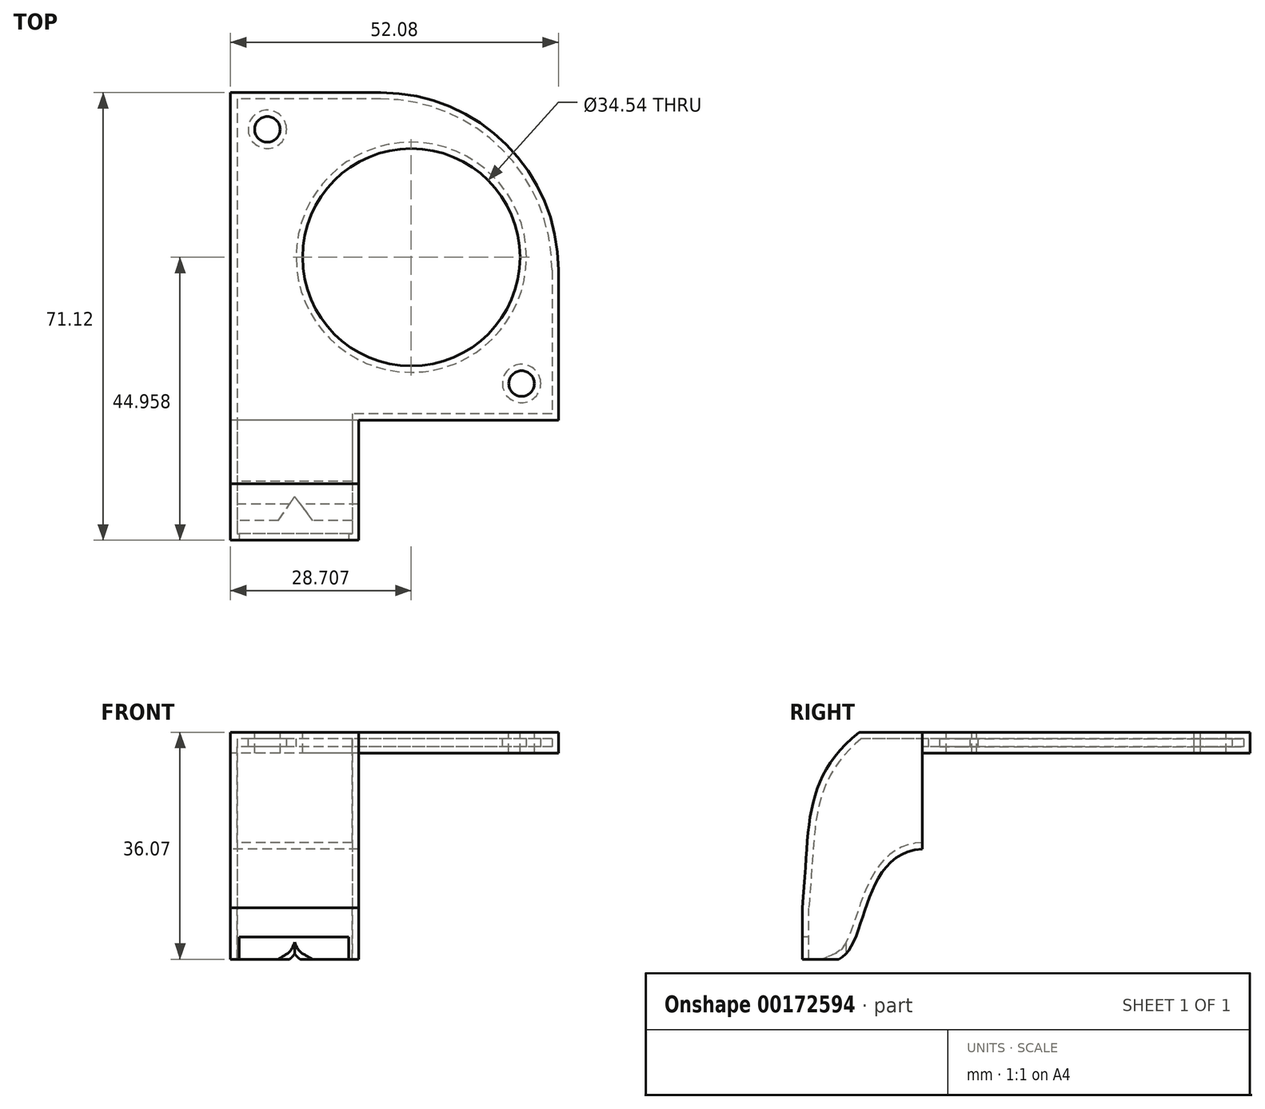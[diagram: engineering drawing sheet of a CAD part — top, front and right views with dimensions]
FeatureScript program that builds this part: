
annotation { "Feature Type Name" : "Feature", "Feature Type Description" : "" }
export const myFeature = defineFeature(function(context is Context, id is Id, definition is map)
    precondition{}
    {
        {
            var Q0;
            Q0=qCreatedBy(makeId("Front.planeOp"),FACE);
            var sketch = newSketch(context, id + "F0", { "sketchPlane" : qUnion([Q0])});
            skLineSegment(sketch, "E0.bottom", {"start": v(26.04, 1.65) * mm, "end": v(-26.04, 1.65) * mm});
            skLineSegment(sketch, "E0.top", {"start": v(26.04, -1.65) * mm, "end": v(-26.04, -1.65) * mm});
            skLineSegment(sketch, "E0.left", {"start": v(26.04, 1.65) * mm, "end": v(26.04, -1.65) * mm});
            skLineSegment(sketch, "E0.right", {"start": v(-26.04, 1.65) * mm, "end": v(-26.04, -1.65) * mm});
            skPoint(sketch, "E0.middle", {"position": v(0, 0) * mm});
            skLineSegment(sketch, "E1.bottom", {"start": v(-26.04, -1.65) * mm, "end": v(-5.71, -1.65) * mm});
            skLineSegment(sketch, "E1.top", {"start": v(-26.03, -34.67) * mm, "end": v(-5.71, -34.67) * mm});
            skLineSegment(sketch, "E1.left", {"start": v(-26.04, -1.65) * mm, "end": v(-26.04, -34.67) * mm});
            skLineSegment(sketch, "E1.right", {"start": v(-5.71, -1.65) * mm, "end": v(-5.71, -34.67) * mm});
            skPoint(sketch, "E2.middle", {"position": v(-15.87, -31.48) * mm});
            skPoint(sketch, "E2.middle.positionSnap0", {"position": v(-15.87, -34.67) * mm});
            skPoint(sketch, "E2.centerSnap0", {"position": v(-15.87, -34.67) * mm});
            skSolve(sketch);
        }
        {
            var Q0;
            Q0=makeQuery(id+"F0.imprint","IMPRINT",FACE,{"disambiguationData":[TD([[makeQuery(id+"F0.imprint","IMPRINT",EDGE,{"derivedFrom":sQuery(id+"F0.wireOp",EDGE,"E0.bottom")}),1.0]])]});
            extrude(context, id + "F1", {"entities" : qUnion([Q0]), "oppositeDirection" : true, "depth" : 52.07 * mm});
        }
        {
            var Q0;
            Q0=makeQuery(id+"F1.opExtrude","SWEPT_FACE",FACE,{"disambiguationData":[OSD([sQuery(id+"F0.wireOp",EDGE,"E0.bottom")])]});
            var sketch = newSketch(context, id + "F2", { "sketchPlane" : qUnion([Q0])});
            skCircle(sketch, "E3", {"center": v(20.2, 5.84) * mm, "radius": 2.03 * mm});
            skCircle(sketch, "E4", {"center": v(-20.2, 46.23) * mm, "radius": 2.03 * mm});
            skCircle(sketch, "E5", {"center": v(2.67, 25.9) * mm, "radius": 17.27 * mm});
            skLineSegment(sketch, "E6.bottom", {"start": v(-26.04, 0) * mm, "end": v(-5.7, 0) * mm});
            skLineSegment(sketch, "E6.top", {"start": v(-26.04, -19.05) * mm, "end": v(-5.7, -19.05) * mm});
            skLineSegment(sketch, "E6.left", {"start": v(-26.04, 0) * mm, "end": v(-26.04, -19.05) * mm});
            skLineSegment(sketch, "E6.right", {"start": v(-5.7, 0) * mm, "end": v(-5.7, -19.05) * mm});
            skSolve(sketch);
        }
        {
            var Q0;
            Q0=makeQuery(id+"F2.imprint","IMPRINT",FACE,{"disambiguationData":[TD([[makeQuery(id+"F2.imprint","IMPRINT",EDGE,{"derivedFrom":sQuery(id+"F2.wireOp",EDGE,"E4")}),1.0]])]});
            var Q1;
            Q1=makeQuery(id+"F2.imprint","IMPRINT",FACE,{"disambiguationData":[TD([[makeQuery(id+"F2.imprint","IMPRINT",EDGE,{"derivedFrom":sQuery(id+"F2.wireOp",EDGE,"E5")}),1.0]])]});
            var Q2;
            Q2=makeQuery(id+"F2.imprint","IMPRINT",FACE,{"disambiguationData":[TD([[makeQuery(id+"F2.imprint","IMPRINT",EDGE,{"derivedFrom":sQuery(id+"F2.wireOp",EDGE,"E3")}),1.0]])]});
            extrude(context, id + "F3", {"entities" : qUnion([Q0, Q1, Q2]), "operationType" : NewBodyOperationType.REMOVE, "oppositeDirection" : true, "depth" : 25.4 * mm});
        }
        {
            var Q0;
            Q0=makeQuery(id+"F1.opExtrude","CAP_EDGE",EDGE,{"disambiguationData":[OSD([sQuery(id+"F0.wireOp",EDGE,"E0.left")])],"isStart":false});
            fillet(context, id + "F4", {"entities" : qUnion([Q0]), "radius" : 28.2 * mm, "tangentPropagation" : true, "allowEdgeOverflow" : false});
        }
        {
            var Q0;
            Q0=makeQuery(id+"F2.imprint","IMPRINT",FACE,{"disambiguationData":[TD([[makeQuery(id+"F2.imprint","IMPRINT",EDGE,{"derivedFrom":sQuery(id+"F2.wireOp",EDGE,"E6.bottom")}),1.0]])]});
            extrude(context, id + "F5", {"entities" : qUnion([Q0]), "operationType" : NewBodyOperationType.ADD, "oppositeDirection" : true, "depth" : 36.07 * mm});
        }
        {
            var Q0;
            Q0=makeQuery(id+"F5.boolean.opBoolean","MERGE",FACE,{"derivedFrom":[makeQuery(id+"F1.opExtrude","SWEPT_FACE",FACE,{"disambiguationData":[OSD([sQuery(id+"F0.wireOp",EDGE,"E0.right")])]}),makeQuery(id+"F5.opExtrude","SWEPT_FACE",FACE,{"disambiguationData":[OSD([sQuery(id+"F2.wireOp",EDGE,"E6.left")])]})]});
            var sketch = newSketch(context, id + "F6", { "sketchPlane" : qUnion([Q0])});
            skFitSpline(sketch, "E7", {"points": [v(10.08, 1.65) * mm, v(19.05, -26.28) * mm], "startDerivative": vector(26.9, -22.37) * mm, "endDerivative": vector(3.47, -40.14) * mm});
            skFitSpline(sketch, "E8", {"points": [v(0, -16.9) * mm, v(13.31, -34.42) * mm], "startDerivative": vector(29.7, -1.62) * mm, "endDerivative": vector(14.29, -6.1) * mm});
            skLineSegment(sketch, "E9", {"start": v(0, -16.9) * mm, "end": v(0, -1.65) * mm});
            skSolve(sketch);
        }
        {
            var Q0;
            {var subQ0=sQuery(id+"F6.wireOp",EDGE,"E8");Q0=makeQuery(id+"F6.imprint","IMPRINT",FACE,{"disambiguationData":[TD([[makeQuery(id+"F6.imprint","IMPRINT",EDGE,{"derivedFrom":subQ0}),-1.0]])]});}
            var Q1;
            {var subQ0=sQuery(id+"F6.wireOp",EDGE,"E7");Q1=makeQuery(id+"F6.imprint","IMPRINT",FACE,{"disambiguationData":[TD([[makeQuery(id+"F6.imprint","IMPRINT",EDGE,{"derivedFrom":subQ0}),1.0]])]});}
            extrude(context, id + "F7", {"entities" : qUnion([Q0, Q1]), "operationType" : NewBodyOperationType.REMOVE, "oppositeDirection" : true, "depth" : 25.4 * mm});
        }
        {
            var Q0;
            Q0=makeQuery(id+"F5.opExtrude","SWEPT_FACE",FACE,{"disambiguationData":[OSD([sQuery(id+"F2.wireOp",EDGE,"E6.bottom")])]});
            var Q1;
            Q1=makeQuery(id+"F5.opExtrude","CAP_FACE",FACE,{"disambiguationData":[OSD([sQuery(id+"F2.wireOp",EDGE,"E6.bottom"),sQuery(id+"F2.wireOp",EDGE,"E6.top"),sQuery(id+"F2.wireOp",EDGE,"E6.left"),sQuery(id+"F2.wireOp",EDGE,"E6.right")])],"isStart":false});
            shell(context, id + "F8", {"entities" : qUnion([Q0, Q1]), "thickness" : 1.02 * mm});
        }
        {
            var Q0;
            Q0=makeQuery(id+"F5.opExtrude","SWEPT_FACE",FACE,{"disambiguationData":[OSD([sQuery(id+"F2.wireOp",EDGE,"E6.top")])]});
            var sketch = newSketch(context, id + "F9", { "sketchPlane" : qUnion([Q0])});
            skLineSegment(sketch, "E10.bottom", {"start": v(-7.24, -34.99) * mm, "end": v(-24.68, -34.99) * mm});
            skLineSegment(sketch, "E10.top", {"start": v(-7.24, -30.9) * mm, "end": v(-24.68, -30.9) * mm});
            skLineSegment(sketch, "E10.left", {"start": v(-7.24, -34.99) * mm, "end": v(-7.24, -30.9) * mm});
            skLineSegment(sketch, "E10.right", {"start": v(-24.68, -34.99) * mm, "end": v(-24.68, -30.9) * mm});
            skPoint(sketch, "E10.middle", {"position": v(-15.96, -32.95) * mm});
            skSolve(sketch);
        }
        {
            var Q0;
            {var subQ0=sQuery(id+"F9.wireOp",EDGE,"E10.top");Q0=makeQuery(id+"F9.imprint","IMPRINT",FACE,{"disambiguationData":[TD([[makeQuery(id+"F9.imprint","IMPRINT",EDGE,{"derivedFrom":subQ0}),1.0]])]});}
            extrude(context, id + "F10", {"entities" : qUnion([Q0]), "operationType" : NewBodyOperationType.REMOVE, "oppositeDirection" : true, "depth" : 1.52 * mm});
        }
        {
            var Q0;
            Q0=makeQuery(id+"F5.opExtrude","CAP_FACE",FACE,{"disambiguationData":[OSD([sQuery(id+"F2.wireOp",EDGE,"E6.bottom"),sQuery(id+"F2.wireOp",EDGE,"E6.top"),sQuery(id+"F2.wireOp",EDGE,"E6.left"),sQuery(id+"F2.wireOp",EDGE,"E6.right")])],"isStart":false});
            var sketch = newSketch(context, id + "F11", { "sketchPlane" : qUnion([Q0])});
            skLineSegment(sketch, "E11", {"start": v(-15.86, 12.12) * mm, "end": v(-13.03, 15.9) * mm});
            skPoint(sketch, "E11.startSnap0", {"position": v(-15.86, 13.31) * mm});
            skLineSegment(sketch, "E12", {"start": v(-13.03, 15.9) * mm, "end": v(-18.41, 15.9) * mm});
            skLineSegment(sketch, "E13", {"start": v(-18.41, 15.9) * mm, "end": v(-15.86, 12.12) * mm});
            skSolve(sketch);
        }
        {
            var Q0;
            {var subQ0=sQuery(id+"F11.wireOp",EDGE,"E12");Q0=makeQuery(id+"F11.imprint","IMPRINT",FACE,{"disambiguationData":[TD([[makeQuery(id+"F11.imprint","IMPRINT",EDGE,{"derivedFrom":subQ0}),1.0]])]});}
            var Q1;
            {var subQ0=sQuery(id+"F11.wireOp",EDGE,"E13");var subQ1=sQuery(id+"F11.wireOp",EDGE,"E11");var subQ2=makeQuery(id+"F11.imprint","INTERSECT",VERTEX,{"derivedFrom":[subQ1,subQ0]});Q1=makeQuery(id+"F11.imprint","IMPRINT",FACE,{"disambiguationData":[TD([[makeQuery(id+"F11.imprint","IMPRINT",EDGE,{"disambiguationData":[TD([[subQ2,-1.0]])],"derivedFrom":subQ1}),1.0]])]});}
            extrude(context, id + "F12", {"entities" : qUnion([Q0, Q1]), "operationType" : NewBodyOperationType.REMOVE, "oppositeDirection" : true, "depth" : 7.14 * mm});
        }
    });
